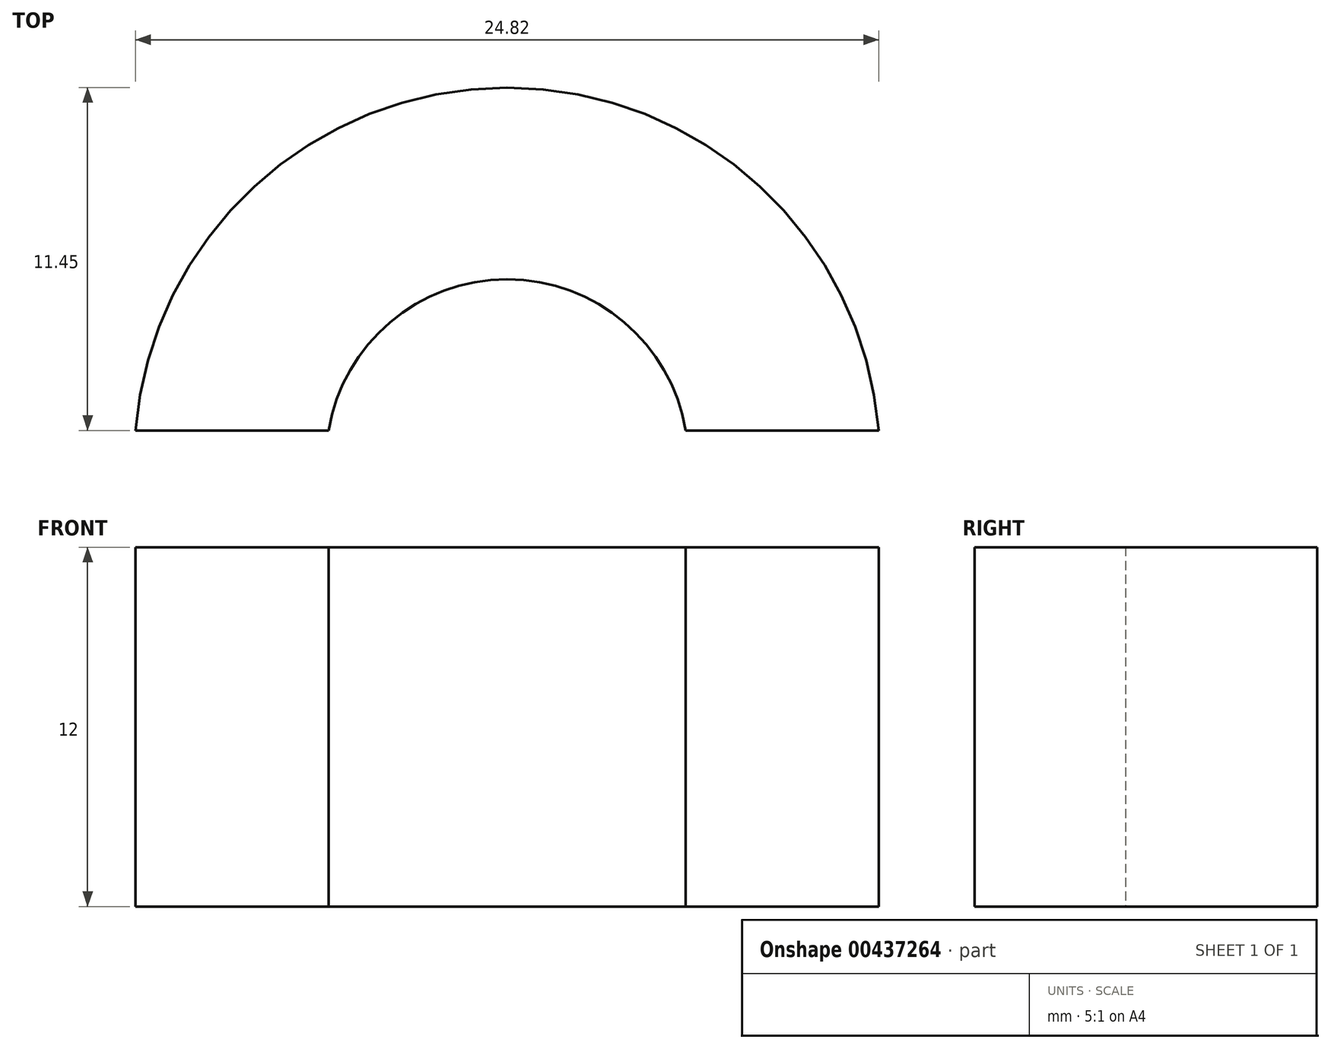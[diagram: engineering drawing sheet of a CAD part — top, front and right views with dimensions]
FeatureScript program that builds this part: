
annotation { "Feature Type Name" : "Feature", "Feature Type Description" : "" }
export const myFeature = defineFeature(function(context is Context, id is Id, definition is map)
    precondition{}
    {
        {
            var Q0;
            Q0=qCreatedBy(makeId("Top.planeOp"),FACE);
            var sketch = newSketch(context, id + "F0", { "sketchPlane" : qUnion([Q0])});
            skArc(sketch, "E0", {"start": v(12.4, 1) * mm, "mid": v(0, 12.45) * mm, "end": v(-12.4, 1) * mm});
            skArc(sketch, "E1", {"start": v(5.97, 1) * mm, "mid": v(0, 6.05) * mm, "end": v(-5.97, 1) * mm});
            skLineSegment(sketch, "E2", {"start": v(-12.45, 0) * mm, "end": v(12.45, 0) * mm, "construction": true});
            skLineSegment(sketch, "E3", {"start": v(-12.4, 1) * mm, "end": v(-5.97, 1) * mm});
            skLineSegment(sketch, "E4.trimOffspring", {"start": v(5.97, 1) * mm, "end": v(12.4, 1) * mm});
            skSolve(sketch);
        }
        {
            var Q0;
            Q0=qSketchRegion(id+"F0",true);
            extrude(context, id + "F1", {"entities" : qUnion([Q0]), "depth" : 12 * mm});
        }
    });
